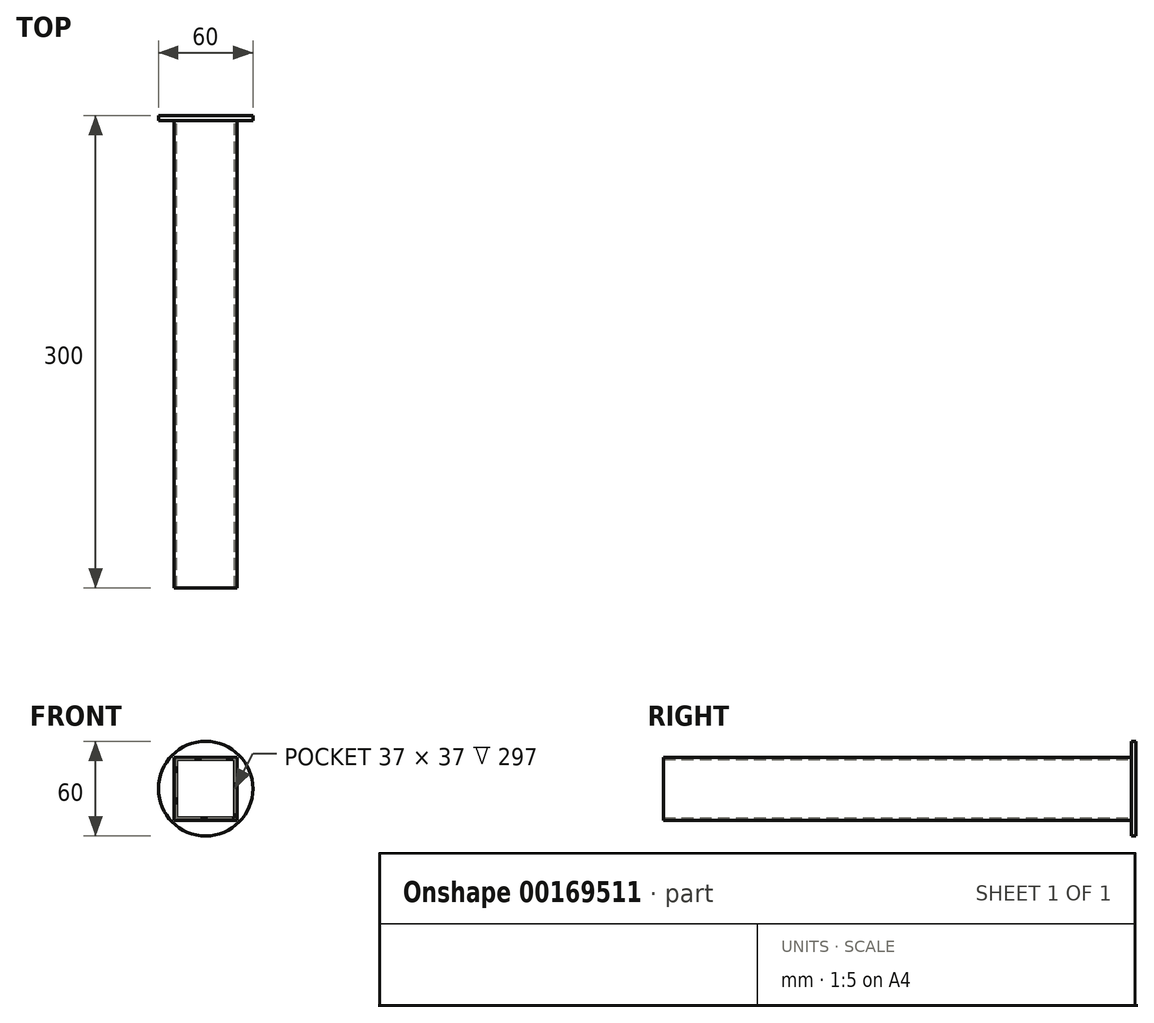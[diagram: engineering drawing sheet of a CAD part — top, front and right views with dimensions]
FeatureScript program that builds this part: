
annotation { "Feature Type Name" : "Feature", "Feature Type Description" : "" }
export const myFeature = defineFeature(function(context is Context, id is Id, definition is map)
    precondition{}
    {
        {
            var Q0;
            Q0=qCreatedBy(makeId("Front.planeOp"),FACE);
            var sketch = newSketch(context, id + "F0", { "sketchPlane" : qUnion([Q0])});
            skLineSegment(sketch, "E0.bottom", {"start": v(20, 20) * mm, "end": v(-20, 20) * mm});
            skLineSegment(sketch, "E0.top", {"start": v(20, -20) * mm, "end": v(-20, -20) * mm});
            skLineSegment(sketch, "E0.left", {"start": v(20, 20) * mm, "end": v(20, -20) * mm});
            skLineSegment(sketch, "E0.right", {"start": v(-20, 20) * mm, "end": v(-20, -20) * mm});
            skPoint(sketch, "E0.middle", {"position": v(0, 0) * mm});
            skLineSegment(sketch, "E1.bottom", {"start": v(18.5, 18.5) * mm, "end": v(-18.5, 18.5) * mm});
            skLineSegment(sketch, "E1.top", {"start": v(18.5, -18.5) * mm, "end": v(-18.5, -18.5) * mm});
            skLineSegment(sketch, "E1.left", {"start": v(18.5, 18.5) * mm, "end": v(18.5, -18.5) * mm});
            skLineSegment(sketch, "E1.right", {"start": v(-18.5, 18.5) * mm, "end": v(-18.5, -18.5) * mm});
            skSolve(sketch);
        }
        {
            var Q0;
            Q0 = qSketchRegion(id + "F0", true);
            extrude(context, id + "F1", {"entities" : qUnion([Q0]), "depth" : 300 * mm});
        }
        {
            var Q0;
            Q0=qCreatedBy(makeId("Front.planeOp"),FACE);
            var sketch = newSketch(context, id + "F2", { "sketchPlane" : qUnion([Q0])});
            skCircle(sketch, "E2", {"center": v(0, 0) * mm, "radius": 30 * mm});
            skSolve(sketch);
        }
        {
            var Q0;
            Q0 = qSketchRegion(id + "F2", true);
            extrude(context, id + "F3", {"entities" : qUnion([Q0]), "operationType" : NewBodyOperationType.ADD, "depth" : 3 * mm});
        }
    });
